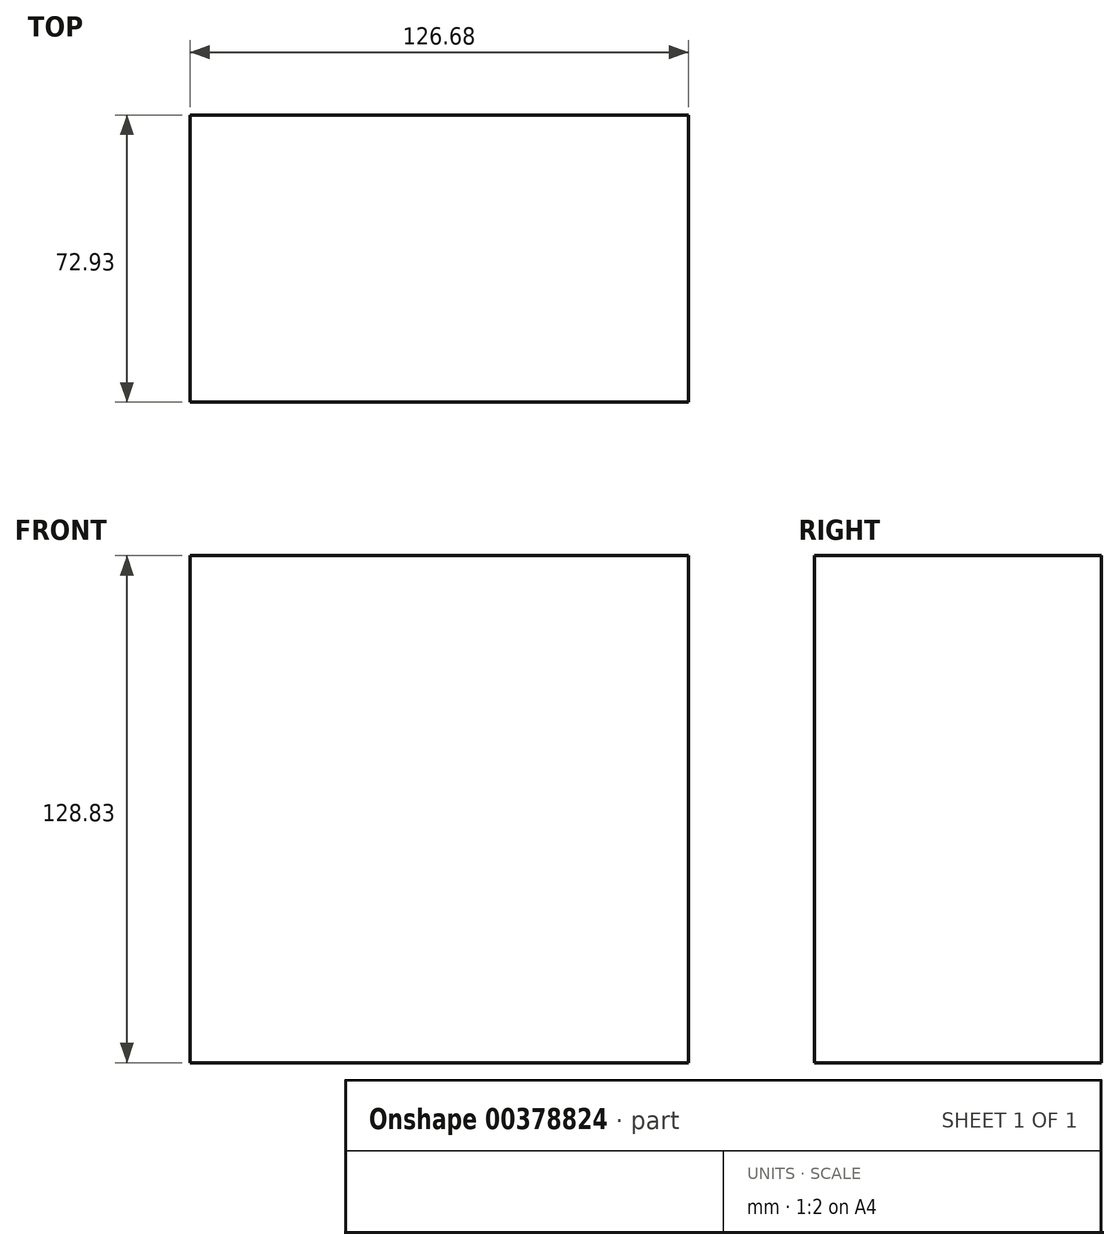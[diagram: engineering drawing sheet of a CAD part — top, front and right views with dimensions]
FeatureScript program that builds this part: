
annotation { "Feature Type Name" : "Feature", "Feature Type Description" : "" }
export const myFeature = defineFeature(function(context is Context, id is Id, definition is map)
    precondition{}
    {
        {
            var Q0;
            Q0=qCreatedBy(makeId("Top.planeOp"),FACE);
            var sketch = newSketch(context, id + "F0", { "sketchPlane" : qUnion([Q0])});
            skLineSegment(sketch, "E0.bottom", {"start": v(-59.29, -22.94) * mm, "end": v(67.39, -22.94) * mm});
            skLineSegment(sketch, "E0.top", {"start": v(-59.29, 49.99) * mm, "end": v(67.39, 49.99) * mm});
            skLineSegment(sketch, "E0.left", {"start": v(-59.29, -22.94) * mm, "end": v(-59.29, 49.99) * mm});
            skLineSegment(sketch, "E0.right", {"start": v(67.39, -22.94) * mm, "end": v(67.39, 49.99) * mm});
            skSolve(sketch);
        }
        {
            var Q0;
            Q0=makeQuery(id+"F0.imprint","IMPRINT",FACE,{"disambiguationData":[TD([[makeQuery(id+"F0.imprint","IMPRINT",EDGE,{"derivedFrom":sQuery(id+"F0.wireOp",EDGE,"E0.bottom")}),1.0]])]});
            extrude(context, id + "F1", {"entities" : qUnion([Q0]), "depth" : 128.83 * mm});
        }
    });
